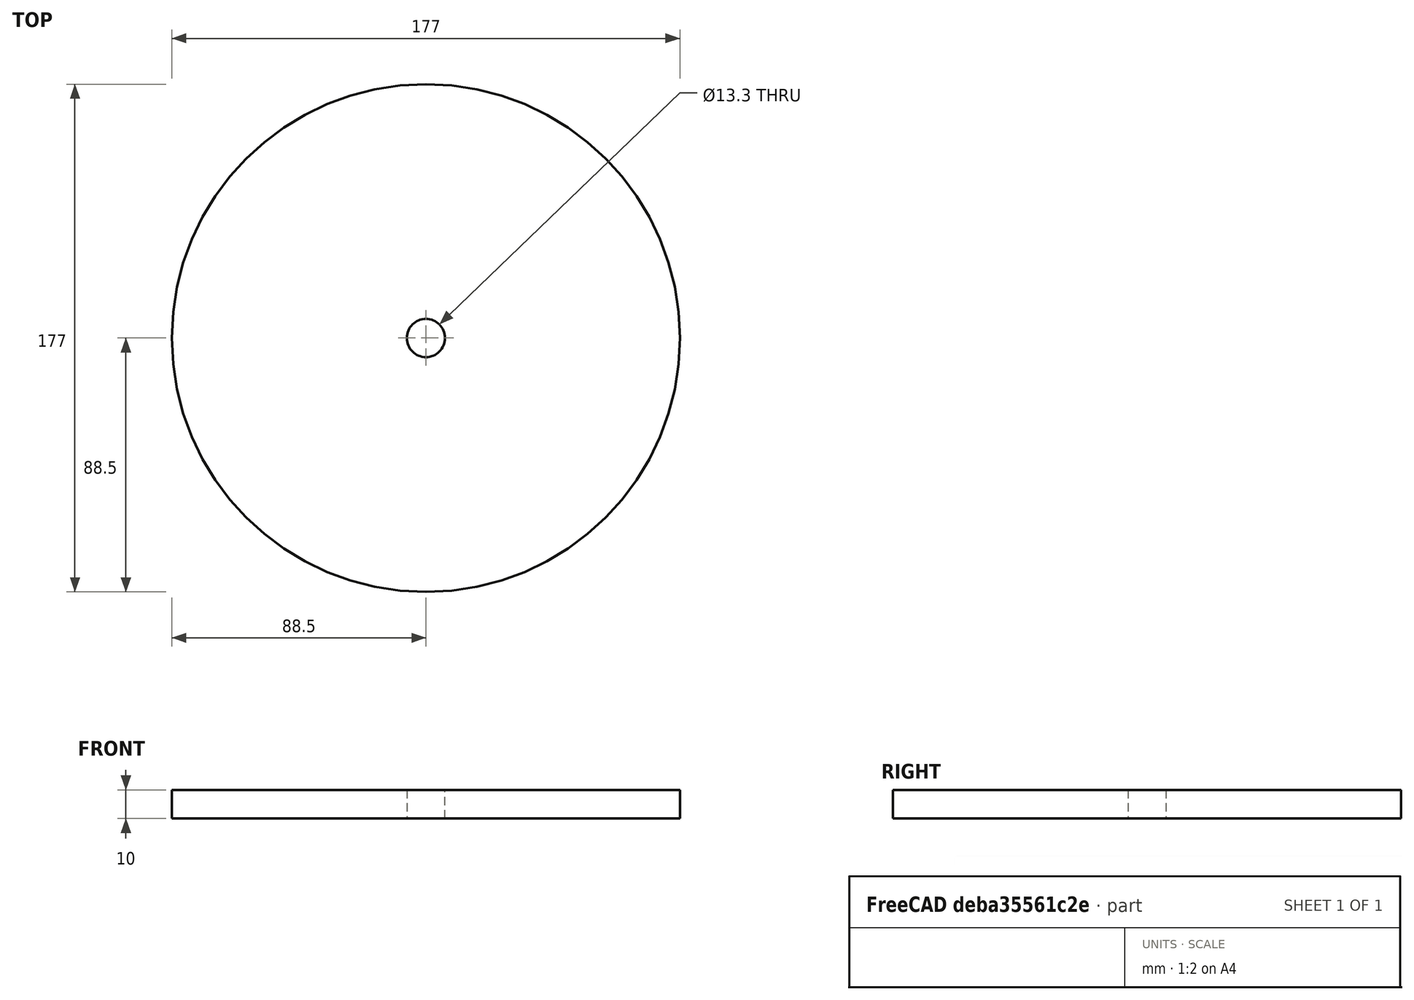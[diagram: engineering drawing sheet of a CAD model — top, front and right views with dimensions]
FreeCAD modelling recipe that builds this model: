
FCSTD DOCUMENT  (FreeCAD 0.19R24291 (Git))
Label: spool
License: All rights reserved
LicenseURL: http://en.wikipedia.org/wiki/All_rights_reserved
objects: Sketcher::SketchObject×1, PartDesign::Pad×1, PartDesign::Body×1
note: 4 computed .brp shape members not serialized (recipe doc carries the construction recipe); baked Part::Feature solids carry a one-line shape summary decoded from their .brp

FEATURE [Sketcher::SketchObject] Sketch
  FullyConstrained = true
  MapMode = 5
  Support = -> [XY_Plane]
  sketch-geometry (2):
    g0: Circle CenterX=0 CenterY=0 CenterZ=0 NormalX=0 NormalY=0 NormalZ=1 AngleXU=0 Radius=6.65
    g1: Circle CenterX=0 CenterY=0 CenterZ=0 NormalX=0 NormalY=0 NormalZ=1 AngleXU=0 Radius=88.5
  constraints (4):
    c: Coincident(g0,g-1)
    c: Coincident(g1,g0)
    c: Diameter(g0) = 13.3
    c: Diameter(g1) = 177
FEATURE [PartDesign::Pad] Pad
  Direction = (1,1,1)
  Length = 10
  Length2 = 100
  Profile = -> Sketch
  Type = 0
FEATURE [PartDesign::Body] Body
  Group = -> [Sketch,Pad]
  Origin = -> Origin
  Tip = -> Pad
